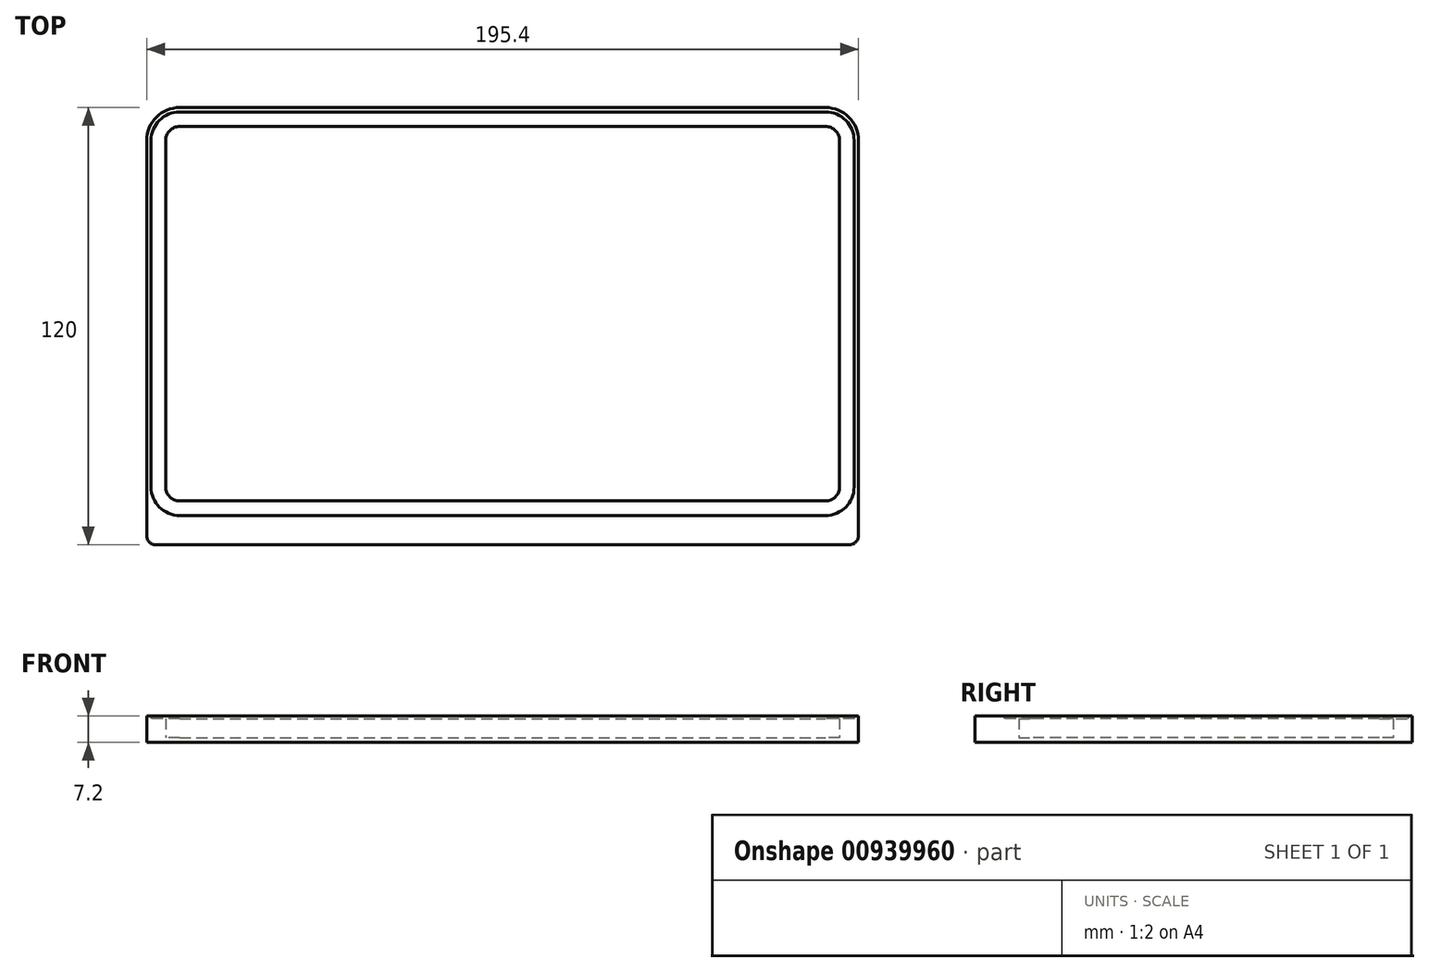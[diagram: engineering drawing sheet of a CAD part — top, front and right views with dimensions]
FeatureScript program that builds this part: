
annotation { "Feature Type Name" : "Feature", "Feature Type Description" : "" }
export const myFeature = defineFeature(function(context is Context, id is Id, definition is map)
    precondition{}
    {
        {
            var Q0;
            Q0=qCreatedBy(makeId("Top.planeOp"),FACE);
            var sketch = newSketch(context, id + "F0", { "sketchPlane" : qUnion([Q0])});
            skLineSegment(sketch, "E0.bottom", {"start": v(-88.64, 56.51) * mm, "end": v(88.64, 56.51) * mm});
            skLineSegment(sketch, "E0.top", {"start": v(-88.64, -54.29) * mm, "end": v(88.64, -54.29) * mm});
            skLineSegment(sketch, "E0.left", {"start": v(-96.5, 48.65) * mm, "end": v(-96.5, -46.43) * mm});
            skLineSegment(sketch, "E0.right", {"start": v(96.5, 48.65) * mm, "end": v(96.5, -46.43) * mm});
            skPoint(sketch, "E1.visualSharp", {"position": v(-96.5, 56.51) * mm});
            skArc(sketch, "E1.filletArc", {"start": v(-88.64, 56.51) * mm, "mid": v(-94.2, 54.2) * mm, "end": v(-96.5, 48.65) * mm});
            skPoint(sketch, "E2.visualSharp", {"position": v(96.5, 56.51) * mm});
            skArc(sketch, "E2.filletArc", {"start": v(96.5, 48.65) * mm, "mid": v(94.2, 54.2) * mm, "end": v(88.64, 56.51) * mm});
            skPoint(sketch, "E3.visualSharp", {"position": v(96.5, -54.29) * mm});
            skArc(sketch, "E3.filletArc", {"start": v(88.64, -54.29) * mm, "mid": v(94.2, -51.99) * mm, "end": v(96.5, -46.43) * mm});
            skPoint(sketch, "E4.visualSharp", {"position": v(-96.5, -54.29) * mm});
            skArc(sketch, "E4.filletArc", {"start": v(-96.5, -46.43) * mm, "mid": v(-94.2, -51.99) * mm, "end": v(-88.64, -54.29) * mm});
            skArc(sketch, "E5.0", {"start": v(-88.64, 52.51) * mm, "mid": v(-91.37, 51.38) * mm, "end": v(-92.5, 48.65) * mm});
            skLineSegment(sketch, "E5.1", {"start": v(-92.5, 48.65) * mm, "end": v(-92.5, -46.43) * mm});
            skLineSegment(sketch, "E5.2", {"start": v(-88.64, 52.51) * mm, "end": v(88.64, 52.51) * mm});
            skArc(sketch, "E5.3", {"start": v(-92.5, -46.43) * mm, "mid": v(-91.37, -49.16) * mm, "end": v(-88.64, -50.29) * mm});
            skArc(sketch, "E5.4", {"start": v(92.5, 48.65) * mm, "mid": v(91.37, 51.38) * mm, "end": v(88.64, 52.51) * mm});
            skLineSegment(sketch, "E5.5", {"start": v(92.5, 48.65) * mm, "end": v(92.5, -46.43) * mm});
            skArc(sketch, "E5.6", {"start": v(88.64, -50.29) * mm, "mid": v(91.37, -49.16) * mm, "end": v(92.5, -46.43) * mm});
            skLineSegment(sketch, "E5.7", {"start": v(-88.64, -50.29) * mm, "end": v(88.64, -50.29) * mm});
            skLineSegment(sketch, "E6.0", {"start": v(-97.7, 48.65) * mm, "end": v(-97.7, -46.43) * mm});
            skLineSegment(sketch, "E6.1", {"start": v(97.7, 48.65) * mm, "end": v(97.7, -46.43) * mm});
            skArc(sketch, "E6.2", {"start": v(97.7, 48.65) * mm, "mid": v(95.05, 55.06) * mm, "end": v(88.64, 57.71) * mm});
            skLineSegment(sketch, "E6.3", {"start": v(-88.64, 57.71) * mm, "end": v(88.64, 57.71) * mm});
            skArc(sketch, "E6.4", {"start": v(-88.64, 57.71) * mm, "mid": v(-95.05, 55.06) * mm, "end": v(-97.7, 48.65) * mm});
            skLineSegment(sketch, "E7", {"start": v(-97.7, -46.43) * mm, "end": v(-97.7, -62.29) * mm});
            skLineSegment(sketch, "E8", {"start": v(-97.7, -62.29) * mm, "end": v(97.7, -62.29) * mm});
            skLineSegment(sketch, "E9", {"start": v(97.7, -62.29) * mm, "end": v(97.7, -46.43) * mm});
            skSolve(sketch);
        }
        {
            var Q0;
            Q0=makeQuery(id+"F0.imprint","IMPRINT",FACE,{"disambiguationData":[TD([[makeQuery(id+"F0.imprint","IMPRINT",EDGE,{"derivedFrom":sQuery(id+"F0.wireOp",EDGE,"E0.bottom")}),-1.0]])]});
            extrude(context, id + "F1", {"entities" : qUnion([Q0]), "depth" : 5.3 * mm, "offsetDistance" : 25 * mm});
        }
        {
            var Q0;
            Q0=makeQuery(id+"F0.imprint","IMPRINT",FACE,{"disambiguationData":[TD([[makeQuery(id+"F0.imprint","IMPRINT",EDGE,{"derivedFrom":sQuery(id+"F0.wireOp",EDGE,"E0.bottom")}),1.0]])]});
            extrude(context, id + "F2", {"entities" : qUnion([Q0]), "operationType" : NewBodyOperationType.ADD, "depth" : 6 * mm, "offsetDistance" : 25 * mm});
        }
        {
            var Q0;
            Q0=makeQuery(id+"F0.imprint","IMPRINT",FACE,{"disambiguationData":[TD([[makeQuery(id+"F0.imprint","IMPRINT",EDGE,{"derivedFrom":sQuery(id+"F0.wireOp",EDGE,"E0.bottom")}),1.0]])]});
            var Q1;
            Q1=makeQuery(id+"F0.imprint","IMPRINT",FACE,{"disambiguationData":[TD([[makeQuery(id+"F0.imprint","IMPRINT",EDGE,{"derivedFrom":sQuery(id+"F0.wireOp",EDGE,"E0.bottom")}),-1.0]])]});
            var Q2;
            Q2=makeQuery(id+"F0.imprint","IMPRINT",FACE,{"disambiguationData":[TD([[makeQuery(id+"F0.imprint","IMPRINT",EDGE,{"derivedFrom":sQuery(id+"F0.wireOp",EDGE,"E5.0")}),1.0]])]});
            extrude(context, id + "F3", {"entities" : qUnion([Q0, Q1, Q2]), "operationType" : NewBodyOperationType.ADD, "depth" : -1.2 * mm, "offsetDistance" : 25 * mm});
        }
        {
            var Q0;
            {var subQ0=sQuery(id+"F0.wireOp",EDGE,"E9");var subQ1=sQuery(id+"F0.wireOp",EDGE,"E8");Q0=makeQuery(id+"F3.boolean.opBoolean","MERGE",EDGE,{"derivedFrom":[makeQuery(id+"F2.opExtrude","SWEPT_EDGE",EDGE,{"disambiguationData":[OSD([subQ1,subQ0])]}),makeQuery(id+"F3.opExtrude","SWEPT_EDGE",EDGE,{"disambiguationData":[OSD([subQ1,subQ0])]})]});}
            var Q1;
            {var subQ0=sQuery(id+"F0.wireOp",EDGE,"E8");var subQ1=sQuery(id+"F0.wireOp",EDGE,"E7");Q1=makeQuery(id+"F3.boolean.opBoolean","MERGE",EDGE,{"derivedFrom":[makeQuery(id+"F2.opExtrude","SWEPT_EDGE",EDGE,{"disambiguationData":[OSD([subQ1,subQ0])]}),makeQuery(id+"F3.opExtrude","SWEPT_EDGE",EDGE,{"disambiguationData":[OSD([subQ1,subQ0])]})]});}
            fillet(context, id + "F4", {"entities" : qUnion([Q0, Q1]), "radius" : 2.5 * mm, "tangentPropagation" : true, "allowEdgeOverflow" : false});
        }
    });
